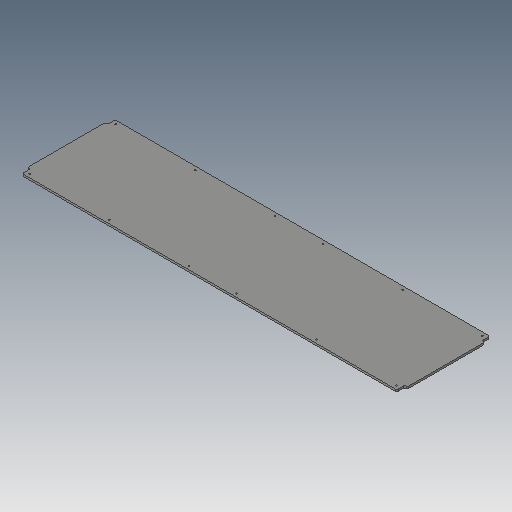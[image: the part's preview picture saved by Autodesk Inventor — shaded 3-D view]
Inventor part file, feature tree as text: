
AUTODESK INVENTOR PART (.ipt)
format: ipt  version: 2023.5 (Build 275446000, 446)  size: 105,472 bytes
history: native  units: in
note: dims shown in document units (in); Inventor stores cm internally (conversion verified against a paired STEP export)
features: fillet x1
ambient origin geometry x8: Origin, YZ Plane, XZ Plane, XY Plane, X Axis, Y Axis, Z Axis, Center Point
bodies: Solid1 (feature_tree)
feature tree (1):
  fillet  "Fillet1"  [1 undecoded]
note: 1 required parameter value undecoded (feature->parameter linkage not recoverable at this tier; creation-order binding heuristic only, values carry confidence <= 0.55)
